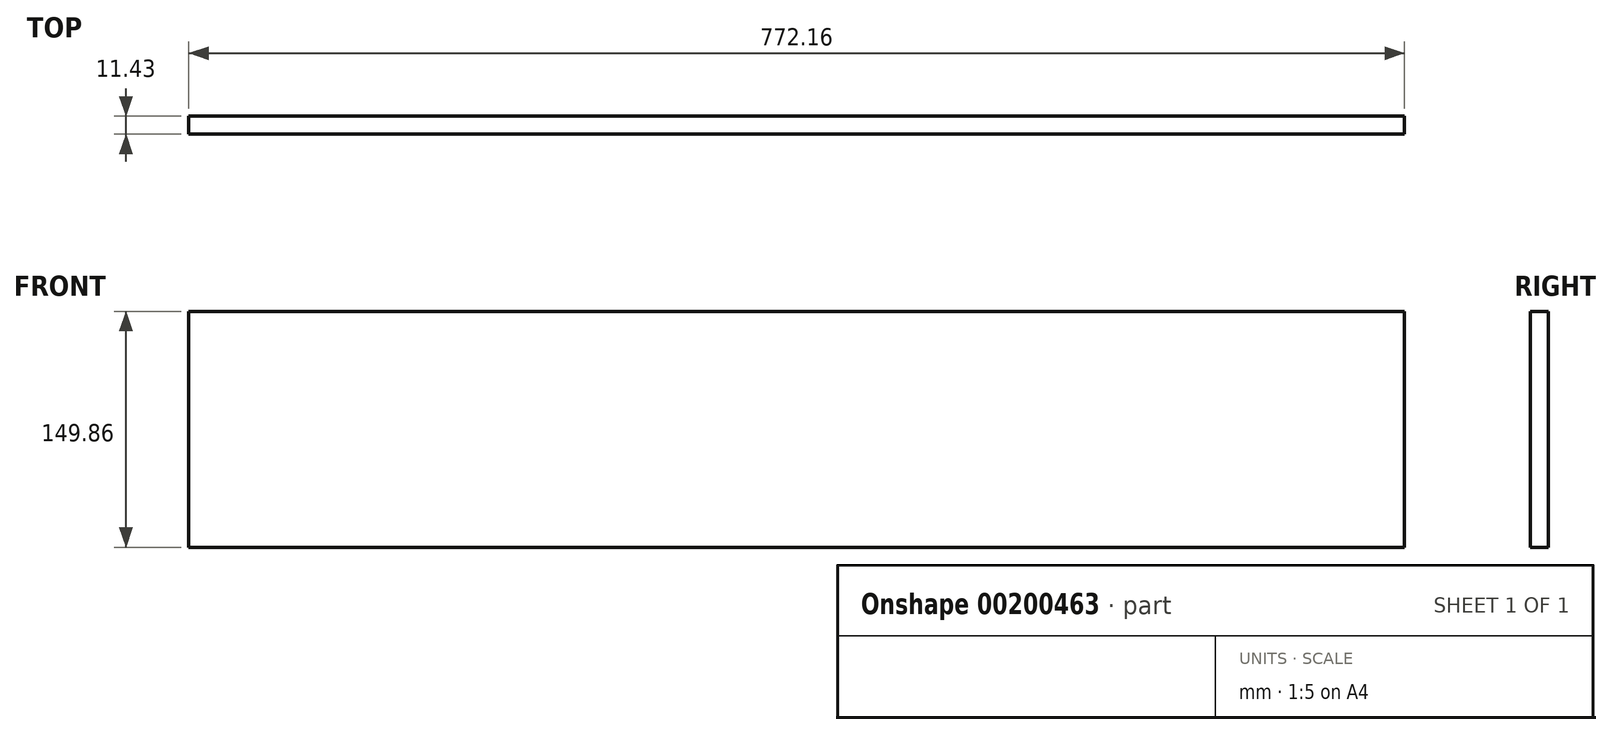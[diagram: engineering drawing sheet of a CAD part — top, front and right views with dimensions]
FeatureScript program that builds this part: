
annotation { "Feature Type Name" : "Feature", "Feature Type Description" : "" }
export const myFeature = defineFeature(function(context is Context, id is Id, definition is map)
    precondition{}
    {
        {
            var Q0;
            Q0=qCreatedBy(makeId("Front.planeOp"),FACE);
            var sketch = newSketch(context, id + "F0", { "sketchPlane" : qUnion([Q0])});
            skLineSegment(sketch, "E0.bottom", {"start": v(-1039.6, 38.06) * mm, "end": v(-267.43, 38.06) * mm});
            skLineSegment(sketch, "E0.top", {"start": v(-1039.6, -111.8) * mm, "end": v(-267.43, -111.8) * mm});
            skLineSegment(sketch, "E0.left", {"start": v(-1039.6, 38.06) * mm, "end": v(-1039.6, -111.8) * mm});
            skLineSegment(sketch, "E0.right", {"start": v(-267.43, 38.06) * mm, "end": v(-267.43, -111.8) * mm});
            skSolve(sketch);
        }
        {
            var Q0;
            Q0 = qSketchRegion(id + "F0", true);
            extrude(context, id + "F1", {"entities" : qUnion([Q0]), "depth" : 11.43 * mm});
        }
    });
